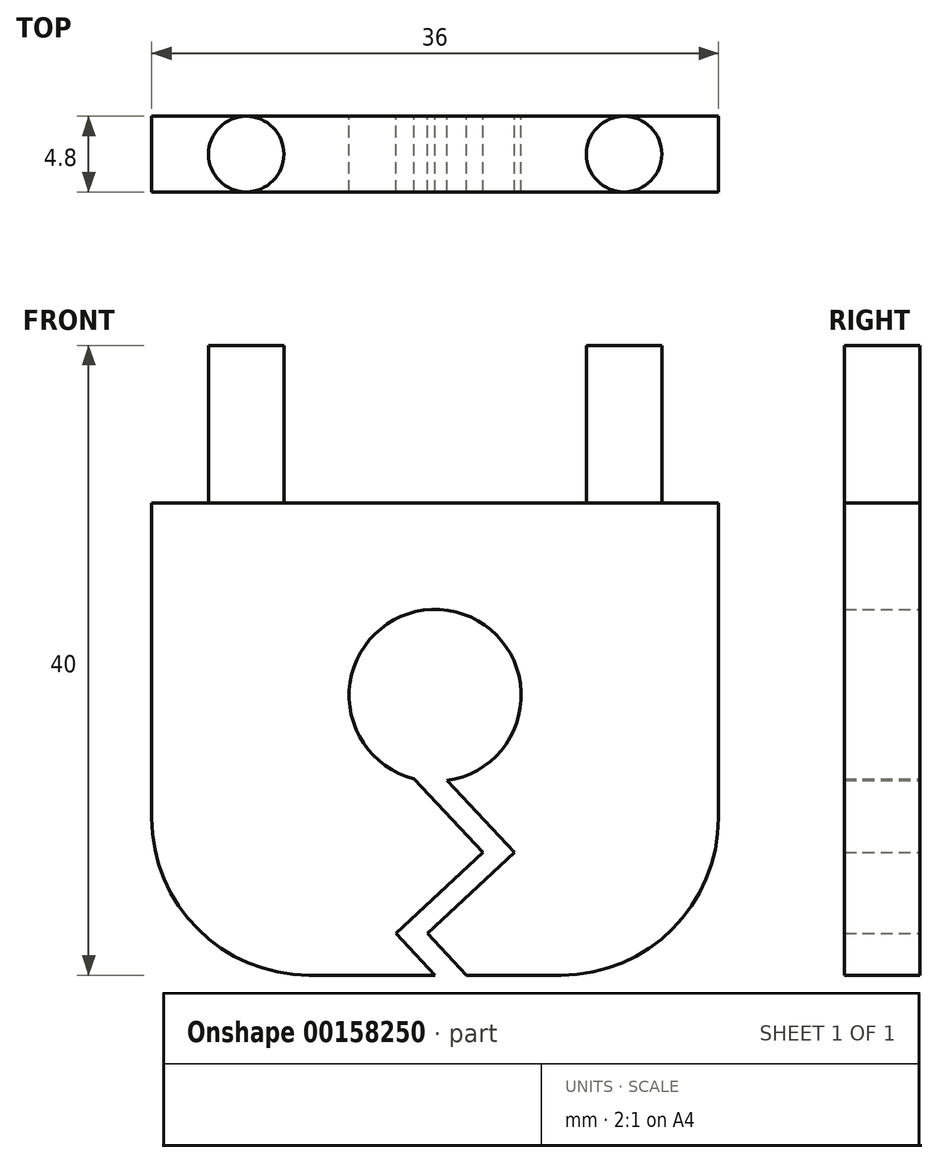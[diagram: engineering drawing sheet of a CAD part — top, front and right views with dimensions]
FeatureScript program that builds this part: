
annotation { "Feature Type Name" : "Feature", "Feature Type Description" : "" }
export const myFeature = defineFeature(function(context is Context, id is Id, definition is map)
    precondition{}
    {
        {
            var Q0;
            Q0=qCreatedBy(makeId("Top.planeOp"),FACE);
            var sketch = newSketch(context, id + "F0", { "sketchPlane" : qUnion([Q0])});
            skCircle(sketch, "E0", {"center": v(-12, 0) * mm, "radius": 2.4 * mm});
            skCircle(sketch, "E1", {"center": v(12, 0) * mm, "radius": 2.4 * mm});
            skSolve(sketch);
        }
        {
            var Q0;
            Q0 = qSketchRegion(id + "F0", true);
            extrude(context, id + "F1", {"entities" : qUnion([Q0]), "depth" : 10 * mm});
        }
        {
            var Q0;
            Q0=qCreatedBy(makeId("Front.planeOp"),FACE);
            var sketch = newSketch(context, id + "F2", { "sketchPlane" : qUnion([Q0])});
            skLineSegment(sketch, "E2.bottom", {"start": v(18, 0) * mm, "end": v(-18, 0) * mm});
            skLineSegment(sketch, "E2.top", {"start": v(18, -30) * mm, "end": v(-18, -30) * mm});
            skLineSegment(sketch, "E2.left", {"start": v(18, 0) * mm, "end": v(18, -30) * mm});
            skLineSegment(sketch, "E2.right", {"start": v(-18, 0) * mm, "end": v(-18, -30) * mm});
            skSolve(sketch);
        }
        {
            var Q0;
            Q0=makeQuery(id+"F2.imprint","IMPRINT",FACE,{"disambiguationData":[TD([[makeQuery(id+"F2.imprint","IMPRINT",EDGE,{"derivedFrom":sQuery(id+"F2.wireOp",EDGE,"E2.bottom")}),1.0]])]});
            extrude(context, id + "F3", {"entities" : qUnion([Q0]), "endBound" : BoundingType.SYMMETRIC, "depth" : 4.8 * mm});
        }
        {
            var Q0;
            Q0=makeQuery(id+"F3.opExtrude","SWEPT_EDGE",EDGE,{"disambiguationData":[OSD([sQuery(id+"F2.wireOp",EDGE,"E2.top"),sQuery(id+"F2.wireOp",EDGE,"E2.left")])]});
            var Q1;
            Q1=makeQuery(id+"F3.opExtrude","SWEPT_EDGE",EDGE,{"disambiguationData":[OSD([sQuery(id+"F2.wireOp",EDGE,"E2.top"),sQuery(id+"F2.wireOp",EDGE,"E2.right")])]});
            fillet(context, id + "F4", {"entities" : qUnion([Q0, Q1]), "radius" : 10 * mm, "tangentPropagation" : true, "allowEdgeOverflow" : false});
        }
        {
            var Q0;
            Q0=makeQuery(id+"F3.opExtrude","CAP_FACE",FACE,{"disambiguationData":[OSD([sQuery(id+"F2.wireOp",EDGE,"E2.bottom"),sQuery(id+"F2.wireOp",EDGE,"E2.top"),sQuery(id+"F2.wireOp",EDGE,"E2.left"),sQuery(id+"F2.wireOp",EDGE,"E2.right")])],"isStart":true});
            var sketch = newSketch(context, id + "F5", { "sketchPlane" : qUnion([Q0])});
            skCircle(sketch, "E3", {"center": v(0, -12.23) * mm, "radius": 5.46 * mm});
            skLineSegment(sketch, "E4", {"start": v(-0.76, -17.64) * mm, "end": v(-5.03, -22.21) * mm});
            skLineSegment(sketch, "E5", {"start": v(-5.03, -22.21) * mm, "end": v(0.48, -27.35) * mm});
            skLineSegment(sketch, "E6", {"start": v(0.48, -27.35) * mm, "end": v(-2, -30) * mm});
            skLineSegment(sketch, "E7", {"start": v(-2, -30) * mm, "end": v(0, -30) * mm});
            skLineSegment(sketch, "E8", {"start": v(0, -30) * mm, "end": v(2.48, -27.35) * mm});
            skLineSegment(sketch, "E9", {"start": v(2.48, -27.35) * mm, "end": v(-3.03, -22.21) * mm});
            skLineSegment(sketch, "E10", {"start": v(-3.03, -22.21) * mm, "end": v(1.34, -17.53) * mm});
            skSolve(sketch);
        }
        {
            var Q0;
            Q0 = qSketchRegion(id + "F5", true);
            extrude(context, id + "F6", {"entities" : qUnion([Q0]), "operationType" : NewBodyOperationType.REMOVE, "oppositeDirection" : true, "depth" : 25 * mm});
        }
    });
